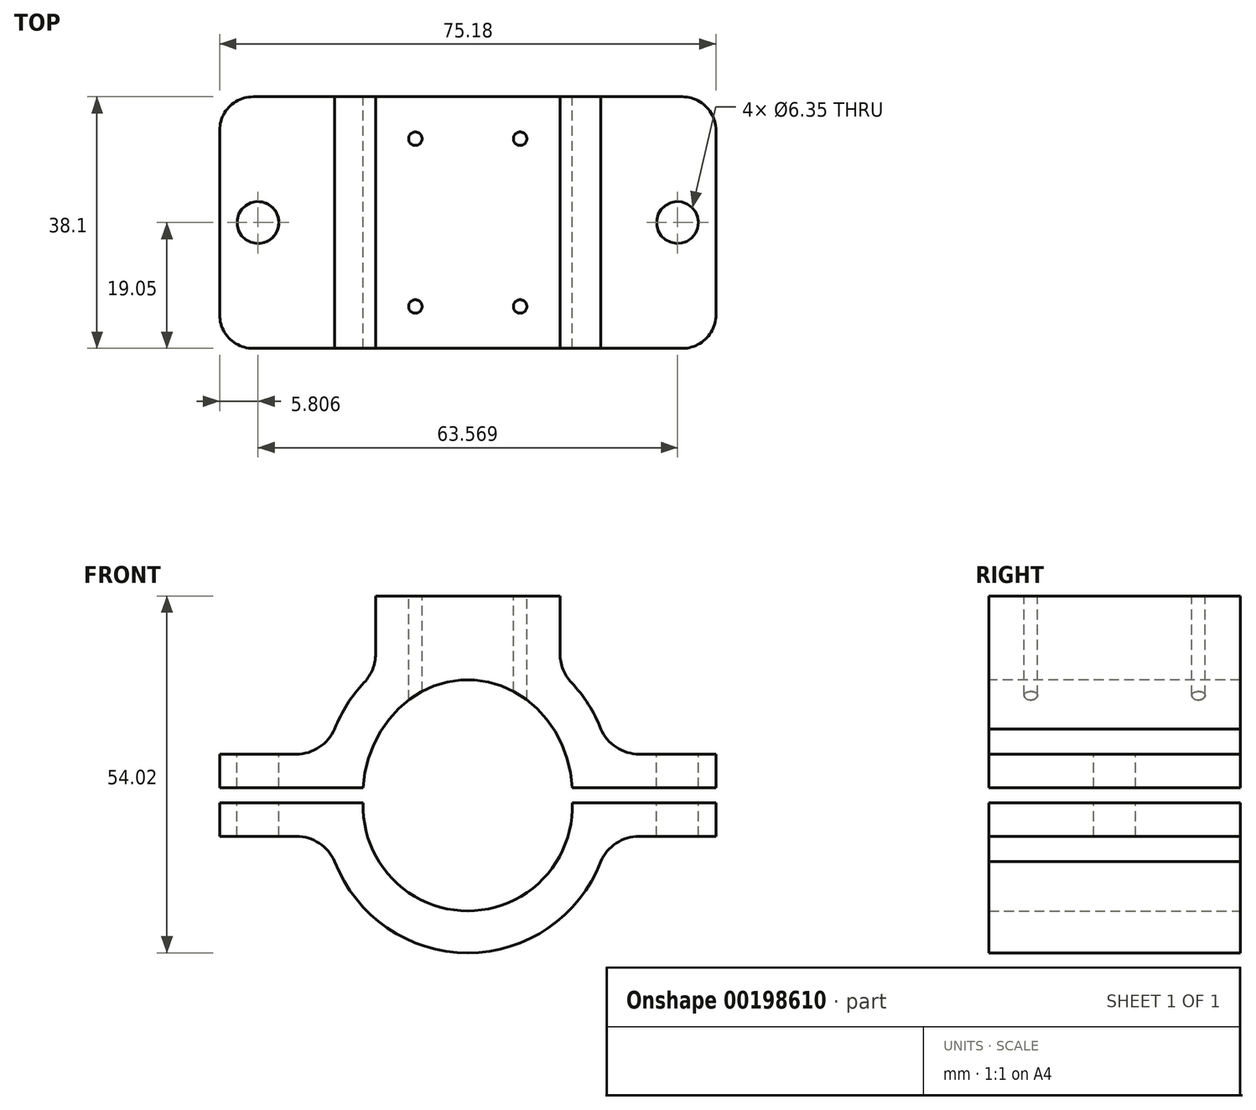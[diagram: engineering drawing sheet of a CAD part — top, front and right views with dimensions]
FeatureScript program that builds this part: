
annotation { "Feature Type Name" : "Feature", "Feature Type Description" : "" }
export const myFeature = defineFeature(function(context is Context, id is Id, definition is map)
    precondition{}
    {
        {
            var Q0;
            Q0=qCreatedBy(makeId("Front.planeOp"),FACE);
            var sketch = newSketch(context, id + "F0", { "sketchPlane" : qUnion([Q0])});
            skEllipticalArc(sketch, "E0", {});
            skLineSegment(sketch, "E1", {"start": v(37.59, 6.22) * mm, "end": v(37.59, 1.14) * mm});
            skLineSegment(sketch, "E2", {"start": v(-37.59, 6.22) * mm, "end": v(-37.59, 1.14) * mm});
            skLineSegment(sketch, "E3", {"start": v(-37.59, 6.22) * mm, "end": v(-25.98, 6.22) * mm});
            skLineSegment(sketch, "E4", {"start": v(25.98, 6.22) * mm, "end": v(37.59, 6.22) * mm});
            skPoint(sketch, "E5.visualSharp", {"position": v(-21.45, 6.22) * mm});
            skArc(sketch, "E5.filletArc", {"start": v(-25.98, 6.22) * mm, "mid": v(-22.5, 7.26) * mm, "end": v(-20.15, 10.05) * mm});
            skPoint(sketch, "E6.visualSharp", {"position": v(21.45, 6.22) * mm});
            skArc(sketch, "E6.filletArc", {"start": v(20.15, 10.05) * mm, "mid": v(22.5, 7.26) * mm, "end": v(25.98, 6.22) * mm});
            skLineSegment(sketch, "E7", {"start": v(37.59, 1.14) * mm, "end": v(15.84, 1.14) * mm});
            skLineSegment(sketch, "E8", {"start": v(-37.59, 1.14) * mm, "end": v(-15.84, 1.14) * mm});
            skLineSegment(sketch, "E9", {"start": v(-13.97, 30.16) * mm, "end": v(13.97, 30.16) * mm});
            skLineSegment(sketch, "E10.MirrorCS", {"start": v(37.59, -1.14) * mm, "end": v(15.84, -1.14) * mm});
            skLineSegment(sketch, "E11.MirrorCS", {"start": v(37.59, -6.22) * mm, "end": v(37.59, -1.14) * mm});
            skLineSegment(sketch, "E12.MirrorCS", {"start": v(25.98, -6.22) * mm, "end": v(37.59, -6.22) * mm});
            skArc(sketch, "E13.MirrorCS", {"start": v(20.15, -10.05) * mm, "mid": v(22.5, -7.26) * mm, "end": v(25.98, -6.22) * mm});
            skLineSegment(sketch, "E14.MirrorCS", {"start": v(-37.59, -1.14) * mm, "end": v(-15.84, -1.14) * mm});
            skLineSegment(sketch, "E15.MirrorCS", {"start": v(-37.59, -6.22) * mm, "end": v(-37.59, -1.14) * mm});
            skLineSegment(sketch, "E16.MirrorCS", {"start": v(-37.59, -6.22) * mm, "end": v(-25.98, -6.22) * mm});
            skArc(sketch, "E17.MirrorCS", {"start": v(-25.98, -6.22) * mm, "mid": v(-22.5, -7.26) * mm, "end": v(-20.15, -10.05) * mm});
            skLineSegment(sketch, "E18", {"start": v(-20.15, -10.05) * mm, "end": v(-20.15, -10.05) * mm});
            skLineSegment(sketch, "E19", {"start": v(20.15, -10.05) * mm, "end": v(20.15, -10.05) * mm});
            skArc(sketch, "E20", {"start": v(-20.15, -10.05) * mm, "mid": v(0, -23.86) * mm, "end": v(20.15, -10.05) * mm});
            skArc(sketch, "E21", {"start": v(20.15, 10.05) * mm, "mid": v(18.27, 13.76) * mm, "end": v(15.7, 17.05) * mm});
            skLineSegment(sketch, "E22", {"start": v(-13.97, 30.16) * mm, "end": v(-13.97, 21.42) * mm});
            skLineSegment(sketch, "E23", {"start": v(13.97, 30.16) * mm, "end": v(13.97, 21.42) * mm});
            skArc(sketch, "E24.trimOffspring", {"start": v(-15.7, 17.05) * mm, "mid": v(-18.27, 13.76) * mm, "end": v(-20.15, 10.05) * mm});
            skArc(sketch, "E25", {"start": v(-15.84, -1.14) * mm, "mid": v(0, -17.51) * mm, "end": v(15.84, -1.14) * mm});
            skPoint(sketch, "E26.visualSharp", {"position": v(13.97, 18.7) * mm});
            skArc(sketch, "E26.filletArc", {"start": v(13.97, 21.42) * mm, "mid": v(14.42, 19.07) * mm, "end": v(15.7, 17.05) * mm});
            skPoint(sketch, "E27.visualSharp", {"position": v(-13.97, 18.7) * mm});
            skArc(sketch, "E27.filletArc", {"start": v(-15.7, 17.05) * mm, "mid": v(-14.42, 19.07) * mm, "end": v(-13.97, 21.42) * mm});
            const initialGuessF0  = {"E0": [0, 0, 0, -1, 0.017462500000000002, 0.015875, 1.6362991865672167, 4.64688612061237]};
            skSetInitialGuess(sketch, initialGuessF0);
            skSolve(sketch);
        }
        {
            var Q0;
            Q0=makeQuery(id+"F0.imprint","IMPRINT",FACE,{"disambiguationData":[TD([[makeQuery(id+"F0.imprint","IMPRINT",EDGE,{"derivedFrom":sQuery(id+"F0.wireOp",EDGE,"E0")}),-1.0]])]});
            var Q1;
            Q1=makeQuery(id+"F0.imprint","IMPRINT",FACE,{"disambiguationData":[TD([[makeQuery(id+"F0.imprint","IMPRINT",EDGE,{"derivedFrom":sQuery(id+"F0.wireOp",EDGE,"E10.MirrorCS")}),1.0]])]});
            extrude(context, id + "F1", {"entities" : qUnion([Q0, Q1]), "depth" : 38.1 * mm});
        }
        {
            var Q0;
            Q0=makeQuery(id+"F1.opExtrude","SWEPT_FACE",FACE,{"disambiguationData":[OSD([sQuery(id+"F0.wireOp",EDGE,"E3")])]});
            var sketch = newSketch(context, id + "F2", { "sketchPlane" : qUnion([Q0])});
            skPoint(sketch, "E28", {"position": v(-31.78, -19.05) * mm});
            skPoint(sketch, "E28.positionSnap0", {"position": v(-37.59, -19.05) * mm});
            skPoint(sketch, "E28.positionSnap1", {"position": v(-31.78, 0) * mm});
            skLineSegment(sketch, "E29.0", {"start": v(25.98, 0) * mm, "end": v(37.59, 0) * mm});
            skLineSegment(sketch, "E29.1", {"start": v(37.59, -38.1) * mm, "end": v(37.59, 0) * mm});
            skPoint(sketch, "E30", {"position": v(31.78, -19.05) * mm});
            skPoint(sketch, "E30.positionSnap0", {"position": v(37.59, -19.05) * mm});
            skPoint(sketch, "E30.positionSnap1", {"position": v(31.78, 0) * mm});
            skSolve(sketch);
        }
        {
            var Q0;
            Q0=sQuery(id+"F2.wireOp",VERTEX,"E28");
            var Q1;
            Q1=sQuery(id+"F2.wireOp",VERTEX,"E30");
            var Q2;
            Q2=makeQuery(id+"F1.opExtrude","SWEPT_BODY",BODY,{"disambiguationData":[OSD([sQuery(id+"F0.wireOp",EDGE,"E0"),sQuery(id+"F0.wireOp",EDGE,"E3"),sQuery(id+"F0.wireOp",EDGE,"E4"),sQuery(id+"F0.wireOp",EDGE,"E5.filletArc"),sQuery(id+"F0.wireOp",EDGE,"E6.filletArc"),sQuery(id+"F0.wireOp",EDGE,"E2"),sQuery(id+"F0.wireOp",EDGE,"E1"),sQuery(id+"F0.wireOp",EDGE,"E7"),sQuery(id+"F0.wireOp",EDGE,"E8"),sQuery(id+"F0.wireOp",EDGE,"E9"),sQuery(id+"F0.wireOp",EDGE,"E21"),sQuery(id+"F0.wireOp",EDGE,"E22"),sQuery(id+"F0.wireOp",EDGE,"E23"),sQuery(id+"F0.wireOp",EDGE,"E24.trimOffspring"),sQuery(id+"F0.wireOp",EDGE,"E26.filletArc"),sQuery(id+"F0.wireOp",EDGE,"E27.filletArc")])]});
            var Q3;
            Q3=makeQuery(id+"F1.opExtrude","SWEPT_BODY",BODY,{"disambiguationData":[OSD([sQuery(id+"F0.wireOp",EDGE,"E10.MirrorCS"),sQuery(id+"F0.wireOp",EDGE,"E11.MirrorCS"),sQuery(id+"F0.wireOp",EDGE,"E12.MirrorCS"),sQuery(id+"F0.wireOp",EDGE,"E13.MirrorCS"),sQuery(id+"F0.wireOp",EDGE,"E14.MirrorCS"),sQuery(id+"F0.wireOp",EDGE,"E15.MirrorCS"),sQuery(id+"F0.wireOp",EDGE,"E16.MirrorCS"),sQuery(id+"F0.wireOp",EDGE,"E17.MirrorCS"),sQuery(id+"F0.wireOp",EDGE,"E18"),sQuery(id+"F0.wireOp",EDGE,"E20"),sQuery(id+"F0.wireOp",EDGE,"E25")])]});
            hole(context, id + "F3", {"style" : HoleStyle.SIMPLE, "endStyle" : HoleEndStyle.BLIND, "holeDiameter" : 6.35 * mm, "holeDepth" : 12.7 * mm, "startFromSketch" : true, "locations" : qUnion([Q0, Q1]), "scope" : qUnion([Q2, Q3])});
        }
        {
            var Q0;
            Q0=makeQuery(id+"F1.opExtrude","SWEPT_FACE",FACE,{"disambiguationData":[OSD([sQuery(id+"F0.wireOp",EDGE,"E9")])]});
            var sketch = newSketch(context, id + "F4", { "sketchPlane" : qUnion([Q0])});
            skLineSegment(sketch, "E31.bottom", {"start": v(7.94, -31.75) * mm, "end": v(-7.94, -31.75) * mm});
            skLineSegment(sketch, "E31.top", {"start": v(7.94, -6.35) * mm, "end": v(-7.94, -6.35) * mm});
            skLineSegment(sketch, "E31.left", {"start": v(7.94, -31.75) * mm, "end": v(7.94, -6.35) * mm});
            skLineSegment(sketch, "E31.right", {"start": v(-7.94, -31.75) * mm, "end": v(-7.94, -6.35) * mm});
            skPoint(sketch, "E31.middle", {"position": v(0, -19.05) * mm});
            skPoint(sketch, "E31.middle.positionSnap0", {"position": v(-13.97, -19.05) * mm});
            skPoint(sketch, "E31.centerSnap0", {"position": v(-13.97, -19.05) * mm});
            skSolve(sketch);
        }
        {
            var Q0;
            Q0=sQuery(id+"F4.wireOp",VERTEX,"E31.right.end");
            var Q1;
            Q1=sQuery(id+"F4.wireOp",VERTEX,"E31.left.end");
            var Q2;
            Q2=sQuery(id+"F4.wireOp",VERTEX,"E31.bottom.start");
            var Q3;
            Q3=sQuery(id+"F4.wireOp",VERTEX,"E31.right.start");
            var Q4;
            Q4=makeQuery(id+"F1.opExtrude","SWEPT_BODY",BODY,{"disambiguationData":[OSD([sQuery(id+"F0.wireOp",EDGE,"E0"),sQuery(id+"F0.wireOp",EDGE,"E3"),sQuery(id+"F0.wireOp",EDGE,"E4"),sQuery(id+"F0.wireOp",EDGE,"E5.filletArc"),sQuery(id+"F0.wireOp",EDGE,"E6.filletArc"),sQuery(id+"F0.wireOp",EDGE,"E2"),sQuery(id+"F0.wireOp",EDGE,"E1"),sQuery(id+"F0.wireOp",EDGE,"E7"),sQuery(id+"F0.wireOp",EDGE,"E8"),sQuery(id+"F0.wireOp",EDGE,"E9"),sQuery(id+"F0.wireOp",EDGE,"E21"),sQuery(id+"F0.wireOp",EDGE,"E22"),sQuery(id+"F0.wireOp",EDGE,"E23"),sQuery(id+"F0.wireOp",EDGE,"E24.trimOffspring"),sQuery(id+"F0.wireOp",EDGE,"E26.filletArc"),sQuery(id+"F0.wireOp",EDGE,"E27.filletArc")])]});
            hole(context, id + "F5", {"style" : HoleStyle.SIMPLE, "endStyle" : HoleEndStyle.BLIND, "holeDiameter" : 2.03 * mm, "holeDepth" : 25.4 * mm, "startFromSketch" : true, "locations" : qUnion([Q0, Q1, Q2, Q3]), "scope" : qUnion([Q4])});
        }
        {
            var Q0;
            Q0=makeQuery(id+"F1.opExtrude","CAP_EDGE",EDGE,{"disambiguationData":[OSD([sQuery(id+"F0.wireOp",EDGE,"E15.MirrorCS")])],"isStart":true});
            var Q1;
            Q1=makeQuery(id+"F1.opExtrude","CAP_EDGE",EDGE,{"disambiguationData":[OSD([sQuery(id+"F0.wireOp",EDGE,"E11.MirrorCS")])],"isStart":true});
            var Q2;
            Q2=makeQuery(id+"F1.opExtrude","CAP_EDGE",EDGE,{"disambiguationData":[OSD([sQuery(id+"F0.wireOp",EDGE,"E1")])],"isStart":true});
            var Q3;
            Q3=makeQuery(id+"F1.opExtrude","CAP_EDGE",EDGE,{"disambiguationData":[OSD([sQuery(id+"F0.wireOp",EDGE,"E2")])],"isStart":true});
            var Q4;
            Q4=makeQuery(id+"F1.opExtrude","CAP_EDGE",EDGE,{"disambiguationData":[OSD([sQuery(id+"F0.wireOp",EDGE,"E15.MirrorCS")])],"isStart":false});
            var Q5;
            Q5=makeQuery(id+"F1.opExtrude","CAP_EDGE",EDGE,{"disambiguationData":[OSD([sQuery(id+"F0.wireOp",EDGE,"E2")])],"isStart":false});
            var Q6;
            Q6=makeQuery(id+"F1.opExtrude","CAP_EDGE",EDGE,{"disambiguationData":[OSD([sQuery(id+"F0.wireOp",EDGE,"E1")])],"isStart":false});
            var Q7;
            Q7=makeQuery(id+"F1.opExtrude","CAP_EDGE",EDGE,{"disambiguationData":[OSD([sQuery(id+"F0.wireOp",EDGE,"E11.MirrorCS")])],"isStart":false});
            fillet(context, id + "F6", {"entities" : qUnion([Q0, Q1, Q2, Q3, Q4, Q5, Q6, Q7]), "radius" : 5.08 * mm, "tangentPropagation" : true, "allowEdgeOverflow" : false});
        }
    });
